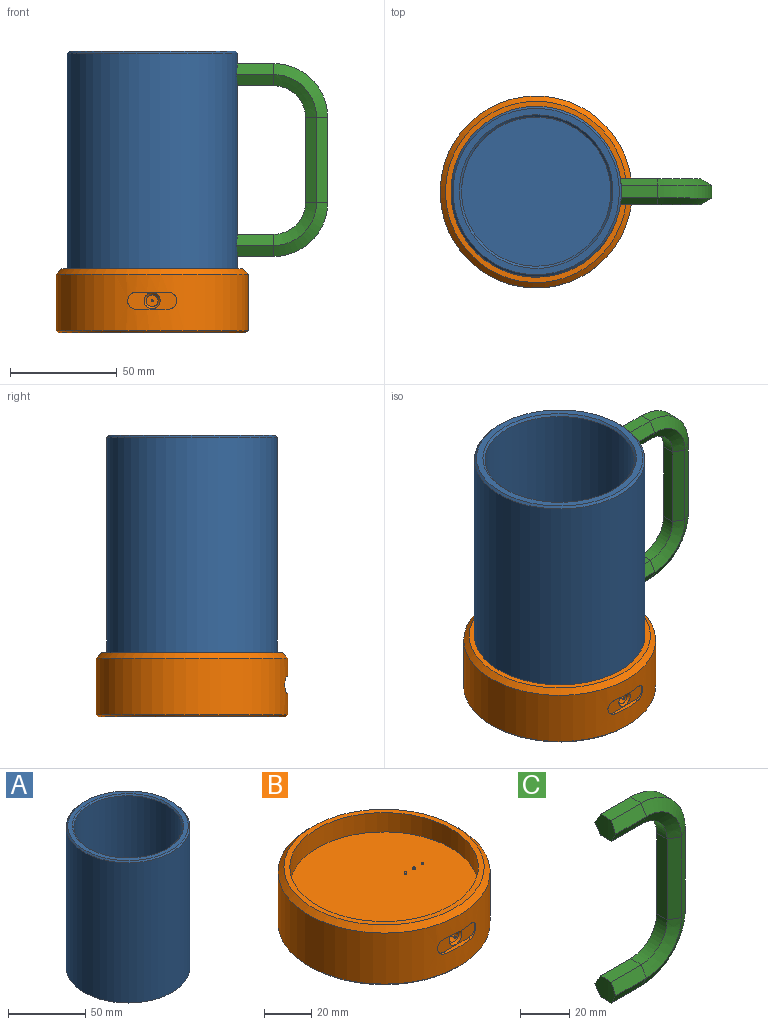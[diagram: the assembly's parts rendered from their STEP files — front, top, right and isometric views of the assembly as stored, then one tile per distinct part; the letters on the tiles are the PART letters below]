
ASSEMBLY  parts=3 mates=2
PART A: 19 faces, bbox 80x80x112 mm
  f0: cylinder r=40mm len=111mm, axis (0,0,-1), area 27897.3mm2, adj f5,f6
  f1: cylinder r=35mm len=79mm, axis (0,0,-1), area 17373mm2, adj f3,f4
  f2: plane 78x78mm, normal (0,0,1), area 706.9mm2, adj f4,f5
  f3: plane 70x70mm, normal (0,0,1), area 3848.5mm2, adj f1
  f4: cone r=35mm half-angle=45deg, axis (0,0,1), area 315.4mm2, adj f1,f2
  f5: cone r=39mm half-angle=45deg, axis (0,0,-1), area 351mm2, adj f0,f2
  f6: plane 80x80mm, normal (0,0,-1), area 3291.6mm2, adj f0,f8
  f7: cylinder r=22.5mm len=45mm, axis (0,0,-1), area 141.4mm2, adj f9,f10
  f8: cylinder r=23.5mm len=47mm, axis (0,0,-1), area 147.7mm2, adj f6,f9
  f9: plane 47x47mm, normal (0,0,-1), area 144.5mm2, adj f7,f8
  f10: plane 45x45mm, normal (0,0,-1), area 515.2mm2, adj f7,f12
  f11: cylinder r=17.5mm len=35mm, axis (0,0,-1), area 110mm2, adj f13,f14
  f12: cylinder r=18.5mm len=37mm, axis (0,0,-1), area 116.2mm2, adj f10,f13
  f13: plane 37x37mm, normal (0,0,-1), area 113.1mm2, adj f11,f12
  f14: plane 35x35mm, normal (0,0,-1), area 389.6mm2, adj f11,f16
  f15: cylinder r=12.5mm len=25mm, axis (0,0,-1), area 78.5mm2, adj f17,f18
  f16: cylinder r=13.5mm len=27mm, axis (0,0,-1), area 84.8mm2, adj f14,f17
  f17: plane 27x27mm, normal (0,0,-1), area 81.7mm2, adj f15,f16
  f18: plane 25x25mm, normal (0,0,-1), area 490.9mm2, adj f15
PART B: 24 faces, bbox 90x90x30 mm
  f0: cylinder r=45mm len=90mm, axis (0,0,-1), area 7320.8mm2, adj f4,f6,f7,f8,f9,f10
  f1: plane 85x85mm, normal (0,0,1), area 648mm2, adj f2,f4
  f2: cylinder r=40mm len=80mm, axis (0,0,1), area 2513.3mm2, adj f1,f3
  f3: plane 80x80mm, normal (0,0,1), area 5024.2mm2, adj f2,f18,f19,f20
  f4: cone r=42.5mm half-angle=45deg, axis (0,0,-1), area 971.9mm2, adj f0,f1
  f5: plane 88x88mm, normal (0,0,-1), area 6082.1mm2, adj f6
  f6: cone r=45mm half-angle=45deg, axis (0,0,1), area 395.4mm2, adj f0,f5
  f7: plane 15x2mm, normal (0,0,-1), area 26.9mm2, adj f0,f8,f10,f11
  f8: cylinder r=4mm len=8mm, axis (0,-1,0), area 10.6mm2, adj f0,f7,f9,f11
  f9: plane 15x2mm, normal (0,0,1), area 26.9mm2, adj f0,f8,f10,f11
  f10: cylinder r=4mm len=8mm, axis (0,-1,0), area 10.6mm2, adj f0,f7,f9,f11
  f11: plane 23x8mm, normal (0,-1,0), area 126.1mm2, adj f7,f8,f9,f10,f16
  f12: cylinder r=2.75mm len=9mm, axis (0,-1,0), area 155.5mm2, adj f13,f16
  f13: plane 5.5x5.5mm, normal (0,-1,0), area 23mm2, adj f12,f14
  f14: cylinder r=0.5mm len=9.75mm, axis (0,1,0), area 30.6mm2, adj f13,f17
  f15: plane 0.5x0.5mm, normal (0,-1,0), area 0.2mm2, adj f17
  f16: cone r=2.75mm half-angle=45deg, axis (0,-1,0), area 28.9mm2, adj f11,f12
  f17: cone r=0.25mm half-angle=45deg, axis (0,1,0), area 0.8mm2, adj f14,f15
  f18: cylinder r=0.5mm len=1mm, axis (0,0,-1), area 1.6mm2, adj f3,f23
  f19: cylinder r=0.5mm len=1mm, axis (0,0,-1), area 1.6mm2, adj f3,f22
  f20: cylinder r=0.5mm len=1mm, axis (0,0,-1), area 1.6mm2, adj f3,f21
  f21: sphere r=0.5mm, area 1.6mm2, adj f20
  f22: sphere r=0.5mm, area 1.6mm2, adj f19
  f23: sphere r=0.5mm, area 1.6mm2, adj f18
PART C: 32 faces, bbox 42.7x12x90.4 mm
  f0: plane 17.19x6mm, normal (0,0,1), area 102.7mm2, adj f1,f5,f6,f31
  f1: plane 17.54x5.21mm, normal (0,-0.87,0.5), area 104.1mm2, adj f0,f2,f7,f31
  f2: plane 17.54x5.21mm, normal (0,-0.87,-0.5), area 104.1mm2, adj f1,f3,f8,f31
  f3: plane 17.19x6mm, normal (0,0,-1), area 102.7mm2, adj f2,f4,f9,f31
  f4: plane 17.54x5.21mm, normal (0,0.87,-0.5), area 104.1mm2, adj f3,f5,f10,f31
  f5: plane 17.54x5.21mm, normal (0,0.87,0.5), area 104.1mm2, adj f0,f4,f11,f31
  f6: cylinder r=14.8mm len=14.8mm, axis (0,-1,0), area 139.5mm2, adj f0,f7,f11,f12
  f7: cone r=14.8mm half-angle=60deg, axis (0,-1,0), area 164mm2, adj f1,f6,f8,f13
  f8: cone r=20mm half-angle=60deg, axis (0,1,0), area 213mm2, adj f2,f7,f9,f14
  f9: cylinder r=25.2mm len=25.2mm, axis (0,-1,0), area 237.5mm2, adj f3,f8,f10,f15
  f10: cone r=25.2mm half-angle=60deg, axis (0,-1,0), area 213mm2, adj f4,f9,f11,f16
  f11: cone r=20mm half-angle=60deg, axis (0,1,0), area 164mm2, adj f5,f6,f10,f17
  f12: plane 40x6mm, normal (-1,0,0), area 240mm2, adj f6,f13,f17,f18
  f13: plane 40x5.2mm, normal (-0.5,-0.87,0), area 240mm2, adj f7,f12,f14,f19
  f14: plane 40x5.2mm, normal (0.5,-0.87,0), area 240mm2, adj f8,f13,f15,f20
  f15: plane 40x6mm, normal (1,0,0), area 240mm2, adj f9,f14,f16,f21
  f16: plane 40x5.2mm, normal (0.5,0.87,0), area 240mm2, adj f10,f15,f17,f22
  f17: plane 40x5.2mm, normal (-0.5,0.87,0), area 240mm2, adj f11,f12,f16,f23
  f18: cylinder r=14.8mm len=14.8mm, axis (0,-1,0), area 139.5mm2, adj f12,f19,f23,f24
  f19: cone r=14.8mm half-angle=60deg, axis (0,-1,0), area 164mm2, adj f13,f18,f20,f25
  f20: cone r=20mm half-angle=60deg, axis (0,1,0), area 213mm2, adj f14,f19,f21,f26
  f21: cylinder r=25.2mm len=25.2mm, axis (0,-1,0), area 237.5mm2, adj f15,f20,f22,f27
  f22: cone r=25.2mm half-angle=60deg, axis (0,-1,0), area 213mm2, adj f16,f21,f23,f28
  f23: cone r=20mm half-angle=60deg, axis (0,1,0), area 164mm2, adj f17,f18,f22,f29
  f24: plane 17.19x6mm, normal (0,0,-1), area 102.7mm2, adj f18,f25,f29,f30
  f25: plane 17.54x5.21mm, normal (0,-0.87,-0.5), area 104.1mm2, adj f19,f24,f26,f30
  f26: plane 17.54x5.21mm, normal (0,-0.87,0.5), area 104.1mm2, adj f20,f25,f27,f30
  f27: plane 17.19x6mm, normal (0,0,1), area 102.7mm2, adj f21,f26,f28,f30
  f28: plane 17.54x5.21mm, normal (0,0.87,0.5), area 104.1mm2, adj f22,f27,f29,f30
  f29: plane 17.54x5.21mm, normal (0,0.87,-0.5), area 104.1mm2, adj f23,f24,f28,f30
  f30: cylinder r=40mm len=12mm, axis (0,0,1), area 93.8mm2, adj f24,f25,f26,f27,f28,f29
  f31: cylinder r=40mm len=12mm, axis (0,0,1), area 93.8mm2, adj f0,f1,f2,f3,f4,f5
PLACE A t=(-106.51,5.56,45)mm
PLACE B at identity
PLACE C t=(37.08,206,41)mm
MATE fastened C.f30 <-> A.f0  axis (0,0,1) through (0,206,121)mm
MATE fastened A.f0 <-> B.f0  axis (0,0,-1) through (0,206,20)mm
